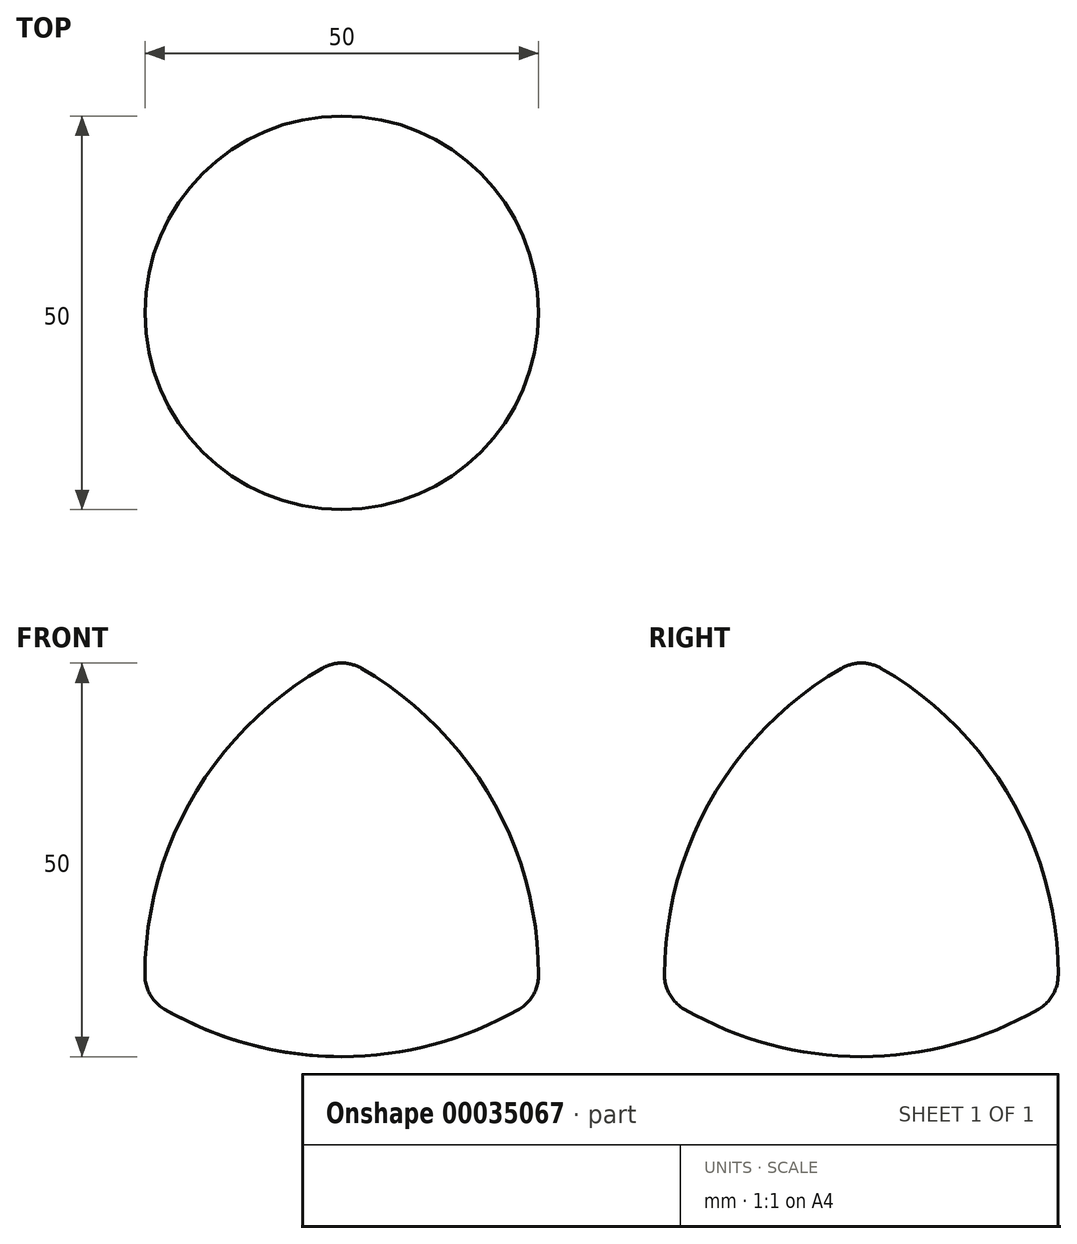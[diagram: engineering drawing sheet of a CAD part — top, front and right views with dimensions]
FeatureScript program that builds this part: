
annotation { "Feature Type Name" : "Feature", "Feature Type Description" : "" }
export const myFeature = defineFeature(function(context is Context, id is Id, definition is map)
    precondition{}
    {
        {
            var Q0;
            Q0=qCreatedBy(makeId("Front.planeOp"),FACE);
            var sketch = newSketch(context, id + "F0", { "sketchPlane" : qUnion([Q0])});
            skArc(sketch, "E0", {"start": v(2.5, 27.42) * mm, "mid": v(0, 28.1) * mm, "end": v(-2.5, 27.42) * mm});
            skArc(sketch, "E1", {"start": v(-2.5, 27.42) * mm, "mid": v(-18.97, 10.95) * mm, "end": v(-25, -11.55) * mm});
            skArc(sketch, "E2", {"start": v(-25, -11.55) * mm, "mid": v(-24.33, -14.05) * mm, "end": v(-22.5, -15.88) * mm});
            skArc(sketch, "E3", {"start": v(-22.5, -15.88) * mm, "mid": v(0, -21.9) * mm, "end": v(22.5, -15.88) * mm});
            skArc(sketch, "E4", {"start": v(22.5, -15.88) * mm, "mid": v(24.33, -14.05) * mm, "end": v(25, -11.55) * mm});
            skArc(sketch, "E5", {"start": v(25, -11.55) * mm, "mid": v(18.97, 10.95) * mm, "end": v(2.5, 27.42) * mm});
            skLineSegment(sketch, "E6", {"start": v(0, -21.9) * mm, "end": v(0, 0) * mm, "construction": true});
            skLineSegment(sketch, "E7", {"start": v(-18.97, 10.95) * mm, "end": v(0, 0) * mm, "construction": true});
            skLineSegment(sketch, "E8", {"start": v(18.97, 10.95) * mm, "end": v(0, 0) * mm, "construction": true});
            skLineSegment(sketch, "E9", {"start": v(0, 23.1) * mm, "end": v(-20, -11.55) * mm, "construction": true});
            skLineSegment(sketch, "E10", {"start": v(-20, -11.55) * mm, "end": v(20, -11.55) * mm, "construction": true});
            skLineSegment(sketch, "E11", {"start": v(20, -11.55) * mm, "end": v(0, 23.1) * mm, "construction": true});
            skLineSegment(sketch, "E12", {"start": v(0, 28.1) * mm, "end": v(0, -21.9) * mm});
            skSolve(sketch);
        }
        {
            var Q0;
            {var subQ3=sQuery(id+"F0.wireOp",EDGE,"E1");Q0=makeQuery(id+"F0.imprint","IMPRINT",FACE,{"disambiguationData":[TD([[makeQuery(id+"F0.imprint","IMPRINT",EDGE,{"derivedFrom":subQ3}),1.0]])]});}
            var Q1;
            Q1=sQuery(id+"F0.wireOp",EDGE,"E12");
            revolve(context, id + "F1", {"entities" : qUnion([Q0]), "axis" : qUnion([Q1]), "revolveType" : RevolveType.FULL});
        }
    });
